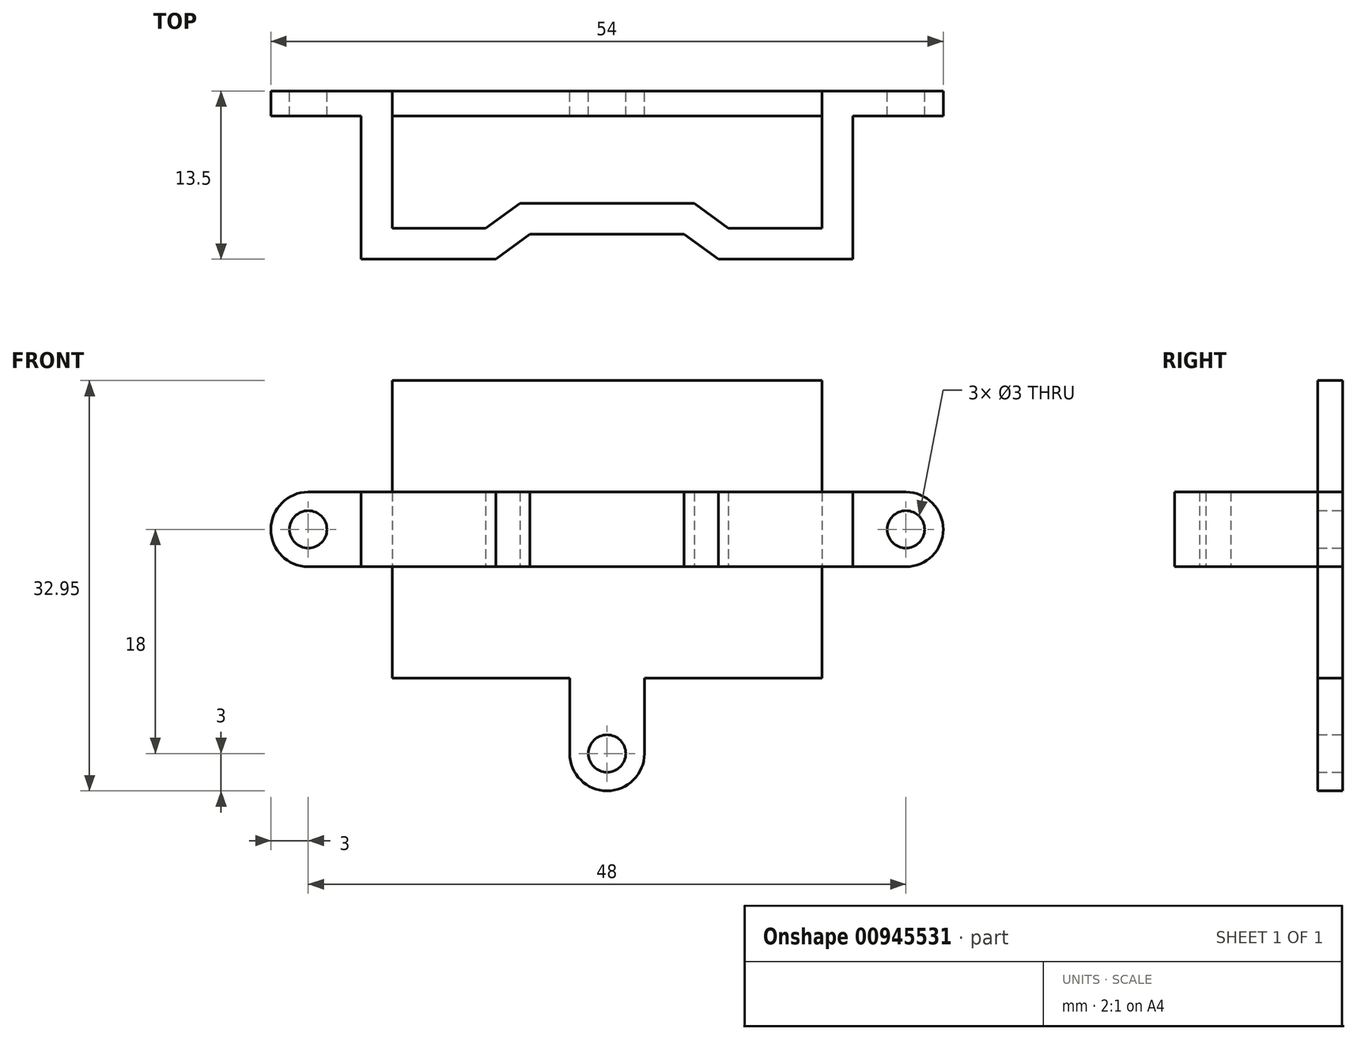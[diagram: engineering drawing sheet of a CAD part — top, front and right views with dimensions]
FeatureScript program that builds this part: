
annotation { "Feature Type Name" : "Feature", "Feature Type Description" : "" }
export const myFeature = defineFeature(function(context is Context, id is Id, definition is map)
    precondition{}
    {
        {
            var Q0;
            Q0=qCreatedBy(makeId("Front.planeOp"),FACE);
            var sketch = newSketch(context, id + "F0", { "sketchPlane" : qUnion([Q0])});
            skLineSegment(sketch, "E0.bottom", {"start": v(17.25, -11.95) * mm, "end": v(3, -11.95) * mm});
            skLineSegment(sketch, "E0.top", {"start": v(17.25, 11.95) * mm, "end": v(-17.25, 11.95) * mm});
            skLineSegment(sketch, "E0.left", {"start": v(17.25, -11.95) * mm, "end": v(17.25, -3) * mm});
            skLineSegment(sketch, "E0.right", {"start": v(-17.25, -11.95) * mm, "end": v(-17.25, -3) * mm});
            skPoint(sketch, "E0.middle", {"position": v(0, 0) * mm});
            skArc(sketch, "E1", {"start": v(-3, -18) * mm, "mid": v(0, -21) * mm, "end": v(3, -18) * mm});
            skArc(sketch, "E2", {"start": v(-24, 3) * mm, "mid": v(-27, 0) * mm, "end": v(-24, -3) * mm});
            skLineSegment(sketch, "E3", {"start": v(0, 7.47) * mm, "end": v(0, -5.14) * mm, "construction": true});
            skArc(sketch, "E4.MirrorC", {"start": v(24, 3) * mm, "mid": v(27, 0) * mm, "end": v(24, -3) * mm});
            skLineSegment(sketch, "E5", {"start": v(-3, -18) * mm, "end": v(-3, -11.95) * mm});
            skLineSegment(sketch, "E6.MirrorCS", {"start": v(3, -18) * mm, "end": v(3, -11.95) * mm});
            skLineSegment(sketch, "E7", {"start": v(-24, 3) * mm, "end": v(-17.25, 3) * mm});
            skLineSegment(sketch, "E8", {"start": v(-4.06, 0) * mm, "end": v(6.3, 0) * mm, "construction": true});
            skLineSegment(sketch, "E9.MirrorCS", {"start": v(-24, -3) * mm, "end": v(-17.25, -3) * mm});
            skLineSegment(sketch, "E10.MirrorCS", {"start": v(24, 3) * mm, "end": v(17.25, 3) * mm});
            skLineSegment(sketch, "E11.MirrorCS", {"start": v(24, -3) * mm, "end": v(17.25, -3) * mm});
            skLineSegment(sketch, "E12.trimOffspring", {"start": v(-17.25, 3) * mm, "end": v(-17.25, 11.95) * mm});
            skLineSegment(sketch, "E13.trimOffspring", {"start": v(-3, -11.95) * mm, "end": v(-17.25, -11.95) * mm});
            skLineSegment(sketch, "E14.trimOffspring", {"start": v(17.25, 3) * mm, "end": v(17.25, 11.95) * mm});
            skCircle(sketch, "E15", {"center": v(-24, 0) * mm, "radius": 1.5 * mm});
            skCircle(sketch, "E16.MirrorC", {"center": v(24, 0) * mm, "radius": 1.5 * mm});
            skCircle(sketch, "E17.MirrorC", {"center": v(0, -18) * mm, "radius": 1.5 * mm});
            skSolve(sketch);
        }
        {
            var Q0;
            Q0 = qSketchRegion(id + "F0", true);
            extrude(context, id + "F1", {"entities" : qUnion([Q0]), "depth" : 2 * mm, "offsetDistance" : 25 * mm});
        }
        {
            var Q0;
            Q0=makeQuery(id+"F1.opExtrude","CAP_FACE",FACE,{"disambiguationData":[OSD([sQuery(id+"F0.wireOp",EDGE,"E0.bottom"),sQuery(id+"F0.wireOp",EDGE,"E0.top"),sQuery(id+"F0.wireOp",EDGE,"E0.left"),sQuery(id+"F0.wireOp",EDGE,"E0.right"),sQuery(id+"F0.wireOp",EDGE,"E1"),sQuery(id+"F0.wireOp",EDGE,"E2"),sQuery(id+"F0.wireOp",EDGE,"E4.MirrorC"),sQuery(id+"F0.wireOp",EDGE,"E5"),sQuery(id+"F0.wireOp",EDGE,"E6.MirrorCS"),sQuery(id+"F0.wireOp",EDGE,"E7"),sQuery(id+"F0.wireOp",EDGE,"E9.MirrorCS"),sQuery(id+"F0.wireOp",EDGE,"E10.MirrorCS"),sQuery(id+"F0.wireOp",EDGE,"E11.MirrorCS"),sQuery(id+"F0.wireOp",EDGE,"E12.trimOffspring"),sQuery(id+"F0.wireOp",EDGE,"E13.trimOffspring"),sQuery(id+"F0.wireOp",EDGE,"E14.trimOffspring"),sQuery(id+"F0.wireOp",EDGE,"E15"),sQuery(id+"F0.wireOp",EDGE,"E16.MirrorC"),sQuery(id+"F0.wireOp",EDGE,"E17.MirrorC")])],"isStart":false});
            var sketch = newSketch(context, id + "F2", { "sketchPlane" : qUnion([Q0])});
            skLineSegment(sketch, "E18.0.0", {"start": v(-17.25, 3) * mm, "end": v(-24, 3) * mm, "construction": true});
            skArc(sketch, "E18.0.1", {"start": v(-24, 3) * mm, "mid": v(-27, 0) * mm, "end": v(-24, -3) * mm, "construction": true});
            skLineSegment(sketch, "E18.0.2", {"start": v(-24, -3) * mm, "end": v(-17.25, -3) * mm, "construction": true});
            skLineSegment(sketch, "E18.0.3", {"start": v(-17.25, -3) * mm, "end": v(-17.25, -11.95) * mm, "construction": true});
            skLineSegment(sketch, "E18.0.4", {"start": v(-17.25, -11.95) * mm, "end": v(-3, -11.95) * mm, "construction": true});
            skLineSegment(sketch, "E18.0.5", {"start": v(-3, -11.95) * mm, "end": v(-3, -18) * mm, "construction": true});
            skArc(sketch, "E18.0.6", {"start": v(-3, -18) * mm, "mid": v(0, -21) * mm, "end": v(3, -18) * mm, "construction": true});
            skLineSegment(sketch, "E18.0.7", {"start": v(3, -18) * mm, "end": v(3, -11.95) * mm, "construction": true});
            skLineSegment(sketch, "E18.0.8", {"start": v(3, -11.95) * mm, "end": v(17.25, -11.95) * mm, "construction": true});
            skLineSegment(sketch, "E18.0.9", {"start": v(17.25, -11.95) * mm, "end": v(17.25, -3) * mm, "construction": true});
            skLineSegment(sketch, "E18.0.10", {"start": v(17.25, -3) * mm, "end": v(24, -3) * mm, "construction": true});
            skArc(sketch, "E18.0.11", {"start": v(24, -3) * mm, "mid": v(27, 0) * mm, "end": v(24, 3) * mm, "construction": true});
            skLineSegment(sketch, "E18.0.12", {"start": v(24, 3) * mm, "end": v(17.25, 3) * mm, "construction": true});
            skLineSegment(sketch, "E18.0.13", {"start": v(17.25, 3) * mm, "end": v(17.25, 11.95) * mm, "construction": true});
            skLineSegment(sketch, "E18.0.14", {"start": v(17.25, 11.95) * mm, "end": v(-17.25, 11.95) * mm, "construction": true});
            skLineSegment(sketch, "E18.0.15", {"start": v(-17.25, 11.95) * mm, "end": v(-17.25, 3) * mm, "construction": true});
            skLineSegment(sketch, "E19.bottom", {"start": v(-17.25, 3) * mm, "end": v(-19.75, 3) * mm});
            skLineSegment(sketch, "E19.top", {"start": v(-17.25, -3) * mm, "end": v(-19.75, -3) * mm});
            skLineSegment(sketch, "E19.left", {"start": v(-17.25, 3) * mm, "end": v(-17.25, -3) * mm});
            skLineSegment(sketch, "E19.right", {"start": v(-19.75, 3) * mm, "end": v(-19.75, -3) * mm});
            skLineSegment(sketch, "E20", {"start": v(0, 6.37) * mm, "end": v(0, -7.57) * mm, "construction": true});
            skLineSegment(sketch, "E21", {"start": v(-6.68, 0) * mm, "end": v(8.1, 0) * mm, "construction": true});
            skLineSegment(sketch, "E22.MirrorCS", {"start": v(17.25, 3) * mm, "end": v(19.75, 3) * mm});
            skLineSegment(sketch, "E23.MirrorCS", {"start": v(17.25, -3) * mm, "end": v(19.75, -3) * mm});
            skLineSegment(sketch, "E24.MirrorCS", {"start": v(17.25, 3) * mm, "end": v(17.25, -3) * mm});
            skLineSegment(sketch, "E25.MirrorCS", {"start": v(19.75, 3) * mm, "end": v(19.75, -3) * mm});
            skSolve(sketch);
        }
        {
            var Q0;
            Q0 = qSketchRegion(id + "F2", true);
            extrude(context, id + "F3", {"entities" : qUnion([Q0]), "operationType" : NewBodyOperationType.ADD, "depth" : 9 * mm, "offsetDistance" : 25 * mm});
        }
        {
            var Q0;
            Q0=qCreatedBy(makeId("Top.planeOp"),FACE);
            var sketch = newSketch(context, id + "F4", { "sketchPlane" : qUnion([Q0])});
            skLineSegment(sketch, "E26.0.0", {"start": v(-24, 0) * mm, "end": v(-17.25, 0) * mm, "construction": true});
            skLineSegment(sketch, "E26.0.1", {"start": v(-17.25, 0) * mm, "end": v(-17.25, -2) * mm, "construction": true});
            skLineSegment(sketch, "E26.0.2", {"start": v(-17.25, -2) * mm, "end": v(-17.25, -11) * mm, "construction": true});
            skLineSegment(sketch, "E26.0.3", {"start": v(-17.25, -11) * mm, "end": v(-19.75, -11) * mm, "construction": true});
            skLineSegment(sketch, "E26.0.4", {"start": v(-19.75, -11) * mm, "end": v(-19.75, -2) * mm, "construction": true});
            skLineSegment(sketch, "E26.0.5", {"start": v(-19.75, -2) * mm, "end": v(-24, -2) * mm, "construction": true});
            skLineSegment(sketch, "E26.0.6", {"start": v(-24, -2) * mm, "end": v(-24, 0) * mm, "construction": true});
            skLineSegment(sketch, "E27.0.0", {"start": v(17.25, 0) * mm, "end": v(24, 0) * mm, "construction": true});
            skLineSegment(sketch, "E27.0.1", {"start": v(24, 0) * mm, "end": v(24, -2) * mm, "construction": true});
            skLineSegment(sketch, "E27.0.2", {"start": v(24, -2) * mm, "end": v(19.75, -2) * mm, "construction": true});
            skLineSegment(sketch, "E27.0.3", {"start": v(19.75, -2) * mm, "end": v(19.75, -11) * mm, "construction": true});
            skLineSegment(sketch, "E27.0.4", {"start": v(19.75, -11) * mm, "end": v(17.25, -11) * mm, "construction": true});
            skLineSegment(sketch, "E27.0.5", {"start": v(17.25, -11) * mm, "end": v(17.25, -2) * mm, "construction": true});
            skLineSegment(sketch, "E27.0.6", {"start": v(17.25, -2) * mm, "end": v(17.25, 0) * mm, "construction": true});
            skLineSegment(sketch, "E28", {"start": v(0, 2.97) * mm, "end": v(0, -5.47) * mm, "construction": true});
            skLineSegment(sketch, "E29", {"start": v(-19.75, -11) * mm, "end": v(-9.75, -11) * mm});
            skLineSegment(sketch, "E30", {"start": v(-9.75, -11) * mm, "end": v(-7, -9) * mm});
            skLineSegment(sketch, "E31", {"start": v(-7, -9) * mm, "end": v(0, -9) * mm});
            skLineSegment(sketch, "E32.0", {"start": v(-6.19, -11.5) * mm, "end": v(0, -11.5) * mm});
            skLineSegment(sketch, "E32.1", {"start": v(-8.94, -13.5) * mm, "end": v(-6.19, -11.5) * mm});
            skLineSegment(sketch, "E32.2", {"start": v(-19.75, -13.5) * mm, "end": v(-8.94, -13.5) * mm});
            skLineSegment(sketch, "E33", {"start": v(-19.75, -11) * mm, "end": v(-19.75, -13.5) * mm});
            skLineSegment(sketch, "E34.MirrorCS", {"start": v(19.75, -11) * mm, "end": v(19.75, -13.5) * mm});
            skLineSegment(sketch, "E35.MirrorCS", {"start": v(8.94, -13.5) * mm, "end": v(6.19, -11.5) * mm});
            skLineSegment(sketch, "E36.MirrorCS", {"start": v(17.25, -11) * mm, "end": v(19.75, -11) * mm, "construction": true});
            skLineSegment(sketch, "E37.MirrorCS", {"start": v(19.75, -13.5) * mm, "end": v(8.94, -13.5) * mm});
            skLineSegment(sketch, "E38.MirrorCS", {"start": v(7, -9) * mm, "end": v(0, -9) * mm});
            skLineSegment(sketch, "E39.MirrorCS", {"start": v(9.75, -11) * mm, "end": v(7, -9) * mm});
            skLineSegment(sketch, "E40.MirrorCS", {"start": v(19.75, -11) * mm, "end": v(9.75, -11) * mm});
            skLineSegment(sketch, "E41.MirrorCS", {"start": v(6.19, -11.5) * mm, "end": v(0, -11.5) * mm});
            skSolve(sketch);
        }
        {
            var Q0;
            Q0 = qSketchRegion(id + "F4", true);
            extrude(context, id + "F5", {"entities" : qUnion([Q0]), "operationType" : NewBodyOperationType.ADD, "endBound" : BoundingType.SYMMETRIC, "depth" : 6 * mm, "offsetDistance" : 25 * mm});
        }
    });
